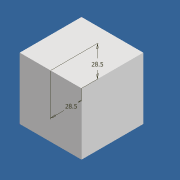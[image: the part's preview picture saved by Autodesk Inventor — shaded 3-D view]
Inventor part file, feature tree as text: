
AUTODESK INVENTOR PART (.ipt)
format: ipt  version: 2020 (Build 240168000, 168)  size: 88,064 bytes
history: native  units: mm
features: sketch x4, extrude x1
ambient origin geometry x8: Origin, YZ Plane, XZ Plane, XY Plane, X Axis, Y Axis, Z Axis, Center Point
bodies: Solid1 (feature_tree)
feature tree (5):
  extrude  "Extrusion1"  Depth=57.0mm
  sketch  "Sketch2"  dims[d2=57.0mm d3=0.0mm]
  sketch  "Sketch3"  dims[d6=8.0mm]
  sketch  "Sketch4"  dims[d7=28.5mm d8=28.5mm d9=19.0mm d10=19.0mm]
  sketch  "Sketch1"  dims[d0=57.0mm d1=57.0mm]
